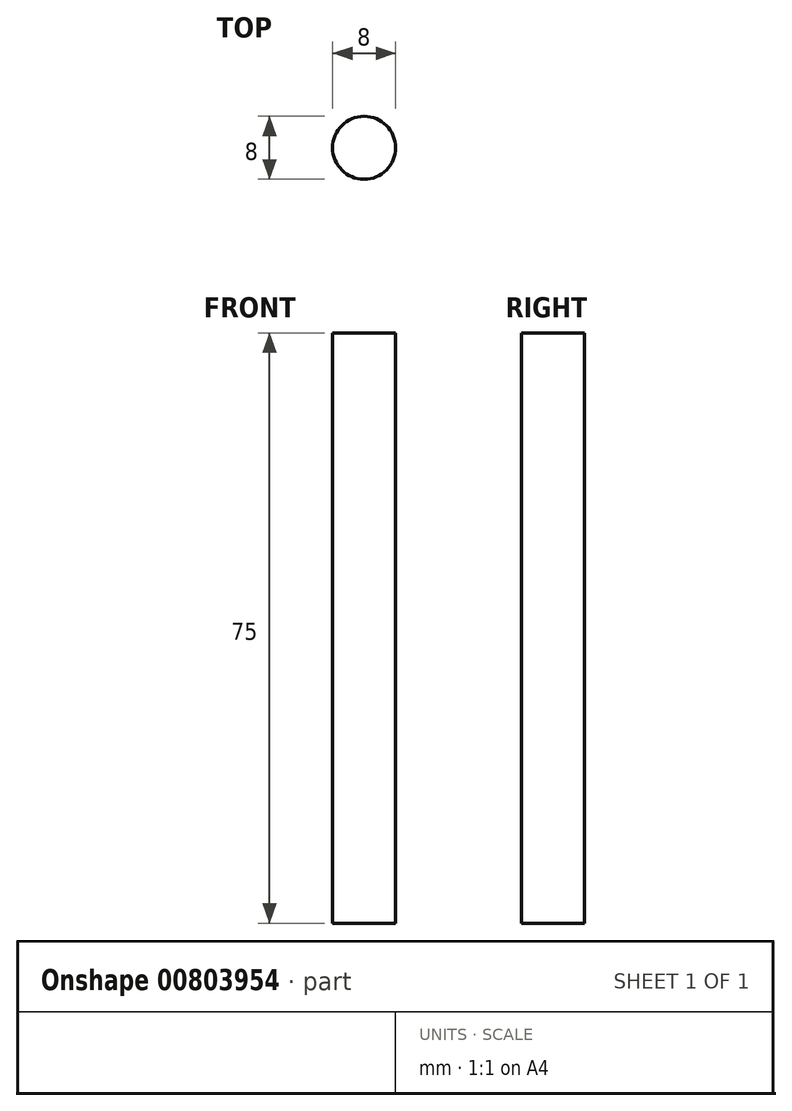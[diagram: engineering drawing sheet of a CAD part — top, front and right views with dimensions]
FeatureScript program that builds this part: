
annotation { "Feature Type Name" : "Feature", "Feature Type Description" : "" }
export const myFeature = defineFeature(function(context is Context, id is Id, definition is map)
    precondition{}
    {
        {
            var Q0;
            Q0=qCreatedBy(makeId("Top.planeOp"),FACE);
            var sketch = newSketch(context, id + "F0", { "sketchPlane" : qUnion([Q0])});
            skCircle(sketch, "E0", {"center": v(0, 0) * mm, "radius": 4 * mm});
            skSolve(sketch);
        }
        {
            var Q0;
            Q0=makeQuery(id+"F0.imprint","IMPRINT",FACE,{"disambiguationData":[TD([[makeQuery(id+"F0.imprint","IMPRINT",EDGE,{"derivedFrom":sQuery(id+"F0.wireOp",EDGE,"E0")}),1.0]])]});
            extrude(context, id + "F1", {"entities" : qUnion([Q0]), "depth" : 75 * mm, "offsetDistance" : 25 * mm});
        }
    });
